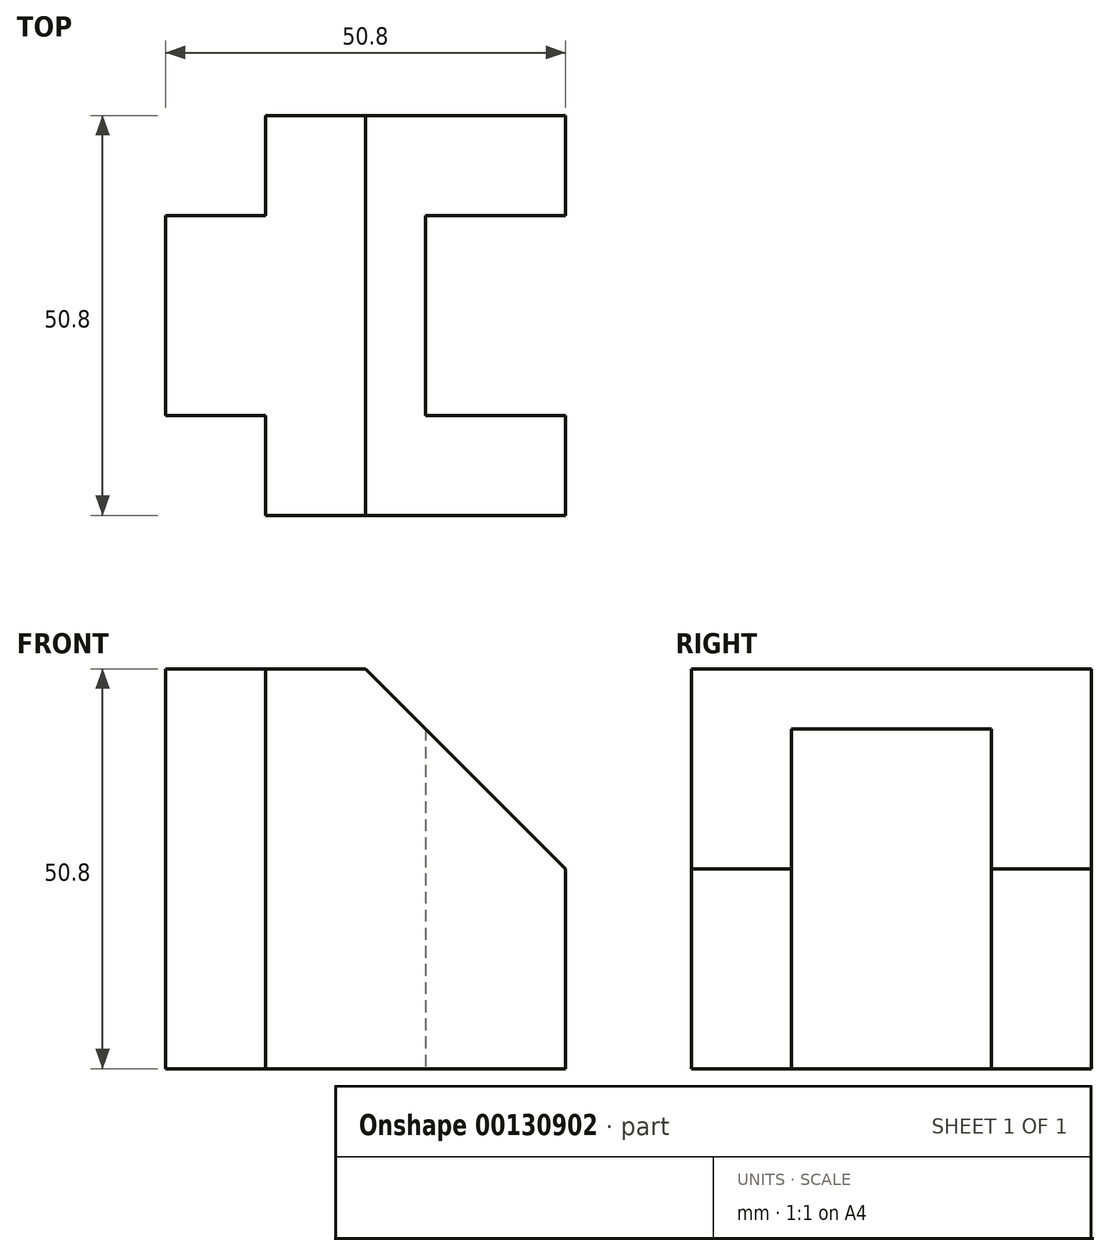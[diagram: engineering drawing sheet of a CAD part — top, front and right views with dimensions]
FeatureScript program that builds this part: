
annotation { "Feature Type Name" : "Feature", "Feature Type Description" : "" }
export const myFeature = defineFeature(function(context is Context, id is Id, definition is map)
    precondition{}
    {
        {
            var Q0;
            Q0=qCreatedBy(makeId("Top.planeOp"),FACE);
            var sketch = newSketch(context, id + "F0", { "sketchPlane" : qUnion([Q0])});
            skLineSegment(sketch, "E0", {"start": v(17.78, -25.4) * mm, "end": v(-20.32, -25.4) * mm});
            skLineSegment(sketch, "E1", {"start": v(-20.32, -25.4) * mm, "end": v(-20.32, -12.7) * mm});
            skLineSegment(sketch, "E2", {"start": v(-20.32, -12.7) * mm, "end": v(-33.02, -12.7) * mm});
            skLineSegment(sketch, "E3", {"start": v(-33.02, -12.7) * mm, "end": v(-33.02, 0) * mm});
            skLineSegment(sketch, "E4", {"start": v(-33.02, 0) * mm, "end": v(-33.02, 12.7) * mm});
            skLineSegment(sketch, "E5", {"start": v(-33.02, 12.7) * mm, "end": v(-20.32, 12.7) * mm});
            skLineSegment(sketch, "E6", {"start": v(-20.32, 12.7) * mm, "end": v(-20.32, 25.4) * mm});
            skLineSegment(sketch, "E7", {"start": v(-20.32, 25.4) * mm, "end": v(17.78, 25.4) * mm});
            skLineSegment(sketch, "E8", {"start": v(17.78, 25.4) * mm, "end": v(17.78, 12.7) * mm});
            skLineSegment(sketch, "E9", {"start": v(17.78, 12.7) * mm, "end": v(0, 12.7) * mm});
            skLineSegment(sketch, "E10", {"start": v(0, 12.7) * mm, "end": v(0, -12.7) * mm});
            skLineSegment(sketch, "E11", {"start": v(0, -12.7) * mm, "end": v(17.78, -12.7) * mm});
            skLineSegment(sketch, "E12", {"start": v(17.78, -12.7) * mm, "end": v(17.78, -25.4) * mm});
            skSolve(sketch);
        }
        {
            var Q0;
            Q0=qSketchRegion(id+"F0",true);
            extrude(context, id + "F1", {"entities" : qUnion([Q0]), "depth" : 50.8 * mm});
        }
        {
            var Q0;
            Q0=makeQuery(id+"F1.opExtrude","SWEPT_FACE",FACE,{"disambiguationData":[OSD([sQuery(id+"F0.wireOp",EDGE,"E0")])]});
            var sketch = newSketch(context, id + "F2", { "sketchPlane" : qUnion([Q0])});
            skLineSegment(sketch, "E13", {"start": v(-7.62, 50.8) * mm, "end": v(17.78, 25.4) * mm});
            skLineSegment(sketch, "E14", {"start": v(17.78, 25.4) * mm, "end": v(17.78, 50.8) * mm});
            skLineSegment(sketch, "E15", {"start": v(17.78, 50.8) * mm, "end": v(-7.62, 50.8) * mm});
            skSolve(sketch);
        }
        {
            var Q0;
            Q0=qSketchRegion(id+"F2",true);
            extrude(context, id + "F3", {"entities" : qUnion([Q0]), "operationType" : NewBodyOperationType.REMOVE, "endBound" : BoundingType.THROUGH_ALL, "oppositeDirection" : true, "depth" : 25.4 * mm});
        }
    });
